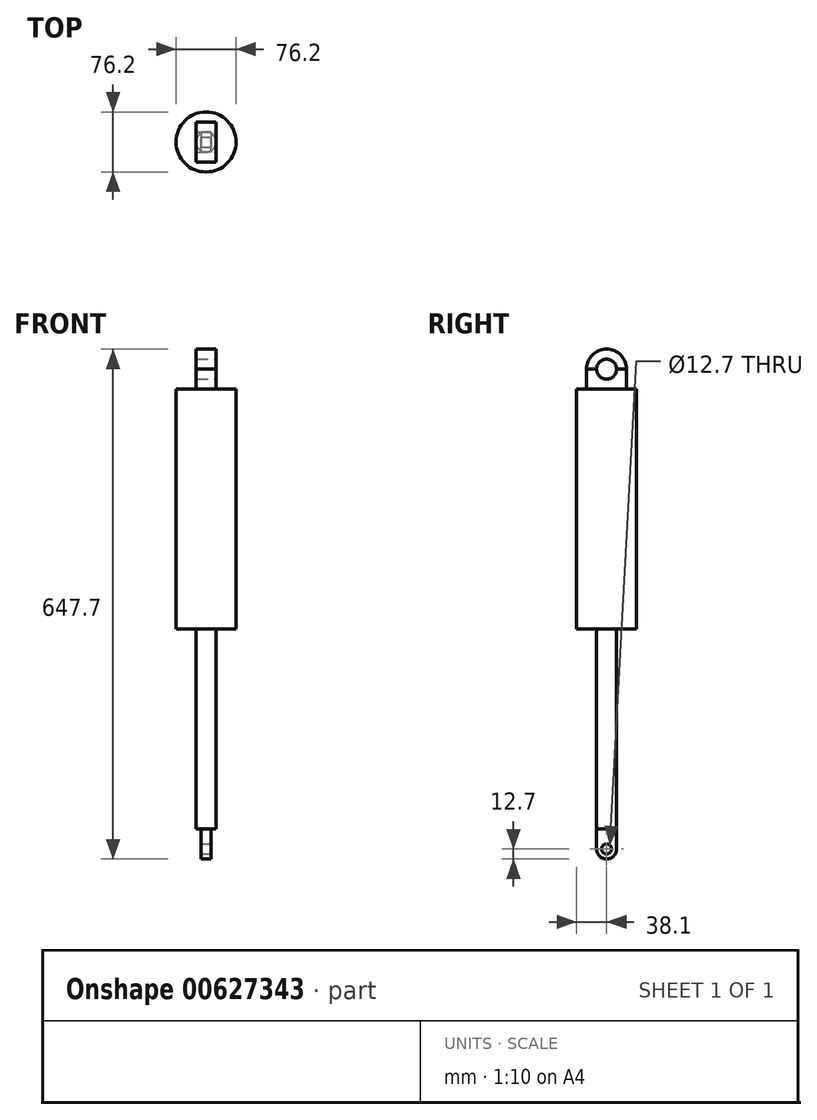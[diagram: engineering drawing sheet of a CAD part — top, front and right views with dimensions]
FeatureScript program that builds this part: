
annotation { "Feature Type Name" : "Feature", "Feature Type Description" : "" }
export const myFeature = defineFeature(function(context is Context, id is Id, definition is map)
    precondition{}
    {
        {
            var Q0;
            Q0=qCreatedBy(makeId("Top.planeOp"),FACE);
            var sketch = newSketch(context, id + "F0", { "sketchPlane" : qUnion([Q0])});
            skCircle(sketch, "E0", {"center": v(0, 0) * mm, "radius": 38.1 * mm});
            skCircle(sketch, "E1", {"center": v(0, 0) * mm, "radius": 12.7 * mm});
            skSolve(sketch);
        }
        {
            var Q0;
            Q0=makeQuery(id+"F0.imprint","IMPRINT",FACE,{"disambiguationData":[TD([[makeQuery(id+"F0.imprint","IMPRINT",EDGE,{"derivedFrom":sQuery(id+"F0.wireOp",EDGE,"E1")}),1.0]])]});
            extrude(context, id + "F1", {"entities" : qUnion([Q0]), "oppositeDirection" : true, "depth" : 254 * mm, "offsetDistance" : 25.4 * mm});
        }
        {
            var Q0;
            Q0=qCreatedBy(makeId("Top.planeOp"),FACE);
            var sketch = newSketch(context, id + "F2", { "sketchPlane" : qUnion([Q0])});
            skCircle(sketch, "E2", {"center": v(0, 0) * mm, "radius": 38.1 * mm});
            skSolve(sketch);
        }
        {
            var Q0;
            Q0=makeQuery(id+"F2.imprint","IMPRINT",FACE,{"disambiguationData":[TD([[makeQuery(id+"F2.imprint","IMPRINT",EDGE,{"derivedFrom":sQuery(id+"F2.wireOp",EDGE,"E2")}),1.0]])]});
            extrude(context, id + "F3", {"entities" : qUnion([Q0]), "operationType" : NewBodyOperationType.ADD, "depth" : 304.8 * mm, "offsetDistance" : 25.4 * mm});
        }
        {
            var Q0;
            Q0=makeQuery(id+"F3.opExtrude","CAP_FACE",FACE,{"disambiguationData":[OSD([sQuery(id+"F2.wireOp",EDGE,"E2")])],"isStart":false});
            var sketch = newSketch(context, id + "F4", { "sketchPlane" : qUnion([Q0])});
            skLineSegment(sketch, "E3.bottom", {"start": v(12.7, -25.4) * mm, "end": v(-12.7, -25.4) * mm});
            skLineSegment(sketch, "E3.top", {"start": v(12.7, 25.4) * mm, "end": v(-12.7, 25.4) * mm});
            skLineSegment(sketch, "E3.left", {"start": v(12.7, -25.4) * mm, "end": v(12.7, 25.4) * mm});
            skLineSegment(sketch, "E3.right", {"start": v(-12.7, -25.4) * mm, "end": v(-12.7, 25.4) * mm});
            skPoint(sketch, "E3.middle", {"position": v(0, 0) * mm});
            skSolve(sketch);
        }
        {
            var Q0;
            Q0=makeQuery(id+"F4.imprint","IMPRINT",FACE,{"disambiguationData":[TD([[makeQuery(id+"F4.imprint","IMPRINT",EDGE,{"derivedFrom":sQuery(id+"F4.wireOp",EDGE,"E3.bottom")}),-1.0]])]});
            extrude(context, id + "F5", {"entities" : qUnion([Q0]), "operationType" : NewBodyOperationType.ADD, "depth" : 25.4 * mm, "offsetDistance" : 25.4 * mm});
        }
        {
            var Q0;
            Q0=makeQuery(id+"F5.opExtrude","SWEPT_FACE",FACE,{"disambiguationData":[OSD([sQuery(id+"F4.wireOp",EDGE,"E3.left")])]});
            var sketch = newSketch(context, id + "F6", { "sketchPlane" : qUnion([Q0])});
            skArc(sketch, "E4", {"start": v(25.4, 330.2) * mm, "mid": v(0, 355.6) * mm, "end": v(-25.4, 330.2) * mm});
            skSolve(sketch);
        }
        {
            var Q0;
            Q0=makeQuery(id+"F6.imprint","IMPRINT",FACE,{"disambiguationData":[TD([[makeQuery(id+"F6.imprint","IMPRINT",EDGE,{"derivedFrom":sQuery(id+"F6.wireOp",EDGE,"E4")}),1.0]])]});
            extrude(context, id + "F7", {"entities" : qUnion([Q0]), "oppositeDirection" : true, "depth" : 25.4 * mm, "offsetDistance" : 25.4 * mm});
        }
        {
            var Q0;
            Q0=makeQuery(id+"F7.opExtrude","CAP_FACE",FACE,{"disambiguationData":[OSD([sQuery(id+"F4.wireOp",EDGE,"E3.left"),sQuery(id+"F6.wireOp",EDGE,"E4")])],"isStart":true});
            var sketch = newSketch(context, id + "F8", { "sketchPlane" : qUnion([Q0])});
            skPoint(sketch, "E5", {"position": v(0, 330.2) * mm});
            skSolve(sketch);
        }
        {
            var Q0;
            Q0=sQuery(id+"F8.wireOp",VERTEX,"E5");
            var Q1;
            Q1=makeQuery(id+"F1.opExtrude","SWEPT_BODY",BODY,{"disambiguationData":[OSD([sQuery(id+"F0.wireOp",EDGE,"E1")])]});
            var Q2;
            Q2=makeQuery(id+"F7.opExtrude","SWEPT_BODY",BODY,{"disambiguationData":[OSD([sQuery(id+"F4.wireOp",EDGE,"E3.left"),sQuery(id+"F6.wireOp",EDGE,"E4")])]});
            hole(context, id + "F9", {"style" : HoleStyle.SIMPLE, "endStyle" : HoleEndStyle.THROUGH, "holeDiameter" : 25.4 * mm, "majorDiameter" : 6.35 * mm, "isTappedThrough" : true, "tappedDepth" : 12.7 * mm, "tapClearance" : 3, "locations" : qUnion([Q0]), "scope" : qUnion([Q1, Q2])});
        }
        {
            var Q0;
            Q0=makeQuery(id+"F1.opExtrude","CAP_FACE",FACE,{"disambiguationData":[OSD([sQuery(id+"F0.wireOp",EDGE,"E1")])],"isStart":false});
            var sketch = newSketch(context, id + "F10", { "sketchPlane" : qUnion([Q0])});
            skLineSegment(sketch, "E6.bottom", {"start": v(6.35, -12.7) * mm, "end": v(-6.35, -12.7) * mm});
            skLineSegment(sketch, "E6.top", {"start": v(6.35, 12.7) * mm, "end": v(-6.35, 12.7) * mm});
            skLineSegment(sketch, "E6.left", {"start": v(6.35, -12.7) * mm, "end": v(6.35, 12.7) * mm});
            skLineSegment(sketch, "E6.right", {"start": v(-6.35, -12.7) * mm, "end": v(-6.35, 12.7) * mm});
            skPoint(sketch, "E6.middle", {"position": v(0, 0) * mm});
            skSolve(sketch);
        }
        {
            var Q0;
            Q0 = qSketchRegion(id + "F10", true);
            extrude(context, id + "F11", {"entities" : qUnion([Q0]), "operationType" : NewBodyOperationType.ADD, "depth" : 25.4 * mm, "offsetDistance" : 25.4 * mm});
        }
        {
            var Q0;
            Q0=makeQuery(id+"F11.opExtrude","SWEPT_FACE",FACE,{"disambiguationData":[OSD([sQuery(id+"F10.wireOp",EDGE,"E6.left")])]});
            var sketch = newSketch(context, id + "F12", { "sketchPlane" : qUnion([Q0])});
            skArc(sketch, "E7", {"start": v(-12.7, -279.4) * mm, "mid": v(0, -292.1) * mm, "end": v(12.7, -279.4) * mm});
            skSolve(sketch);
        }
        {
            var Q0;
            Q0=makeQuery(id+"F12.imprint","IMPRINT",FACE,{"disambiguationData":[TD([[makeQuery(id+"F12.imprint","IMPRINT",EDGE,{"derivedFrom":sQuery(id+"F12.wireOp",EDGE,"E7")}),1.0]])]});
            extrude(context, id + "F13", {"entities" : qUnion([Q0]), "operationType" : NewBodyOperationType.ADD, "oppositeDirection" : true, "depth" : 12.7 * mm, "offsetDistance" : 25.4 * mm});
        }
        {
            var Q0;
            {var subQ0=sQuery(id+"F10.wireOp",EDGE,"E6.left");Q0=makeQuery(id+"F13.boolean.opBoolean","MERGE",FACE,{"derivedFrom":[makeQuery(id+"F11.opExtrude","SWEPT_FACE",FACE,{"disambiguationData":[OSD([subQ0])]}),makeQuery(id+"F13.opExtrude","CAP_FACE",FACE,{"disambiguationData":[OSD([subQ0,sQuery(id+"F12.wireOp",EDGE,"E7")])],"isStart":true})]});}
            var sketch = newSketch(context, id + "F14", { "sketchPlane" : qUnion([Q0])});
            skPoint(sketch, "E8", {"position": v(0, -279.4) * mm});
            skSolve(sketch);
        }
        {
            var Q0;
            Q0=sQuery(id+"F14.wireOp",VERTEX,"E8");
            var Q1;
            Q1=makeQuery(id+"F1.opExtrude","SWEPT_BODY",BODY,{"disambiguationData":[OSD([sQuery(id+"F0.wireOp",EDGE,"E1")])]});
            hole(context, id + "F15", {"style" : HoleStyle.SIMPLE, "endStyle" : HoleEndStyle.THROUGH, "holeDiameter" : 12.7 * mm, "majorDiameter" : 6.35 * mm, "isTappedThrough" : true, "tappedDepth" : 12.7 * mm, "tapClearance" : 3, "locations" : qUnion([Q0]), "scope" : qUnion([Q1])});
        }
    });
